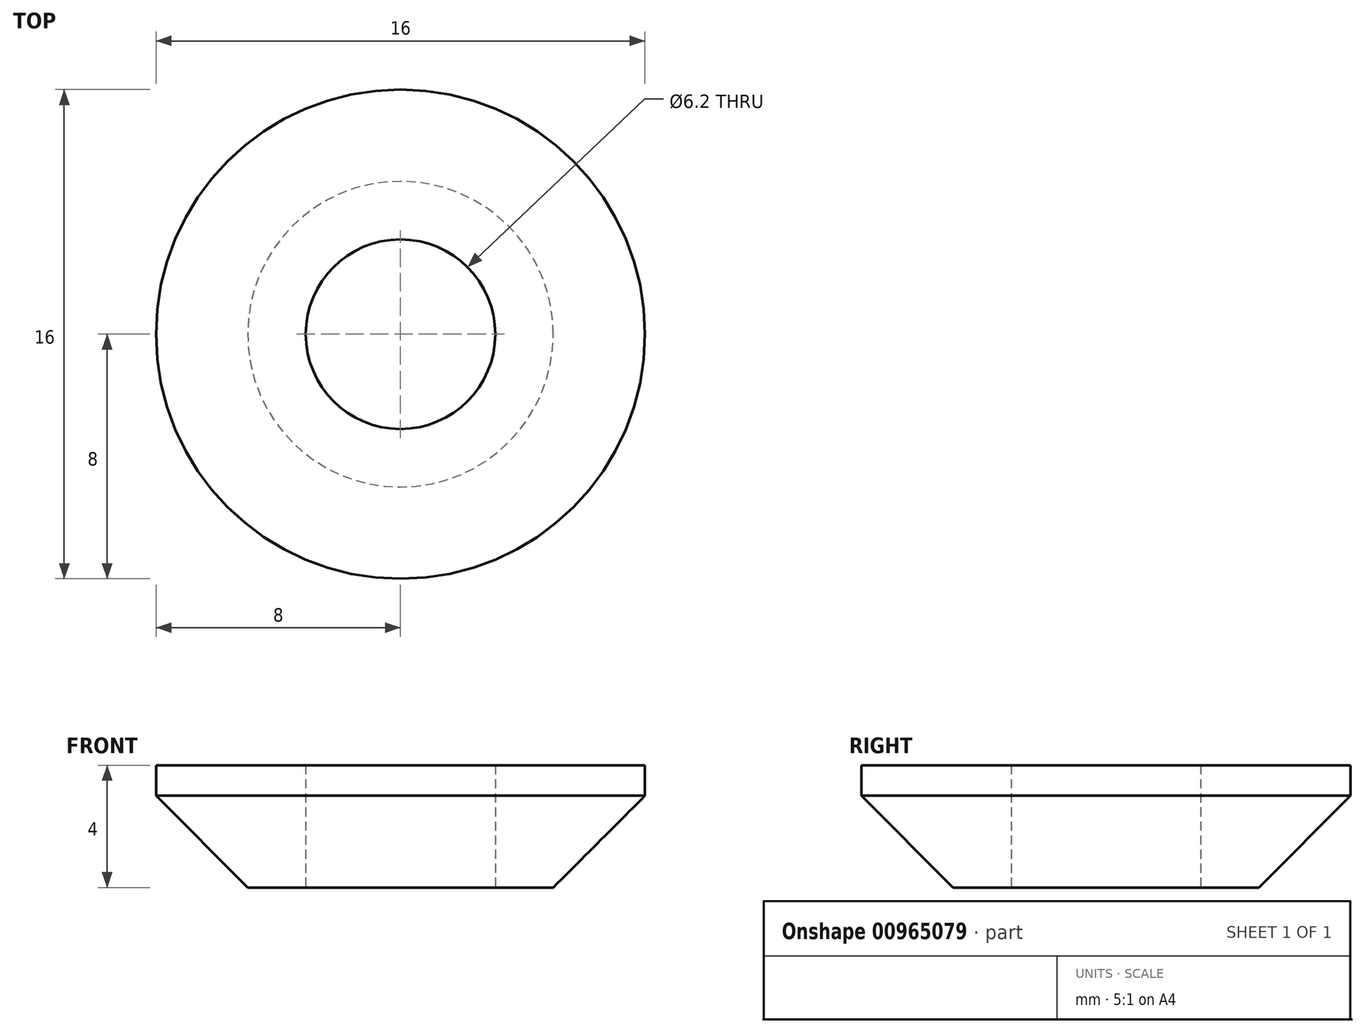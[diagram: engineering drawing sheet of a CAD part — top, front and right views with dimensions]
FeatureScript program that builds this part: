
annotation { "Feature Type Name" : "Feature", "Feature Type Description" : "" }
export const myFeature = defineFeature(function(context is Context, id is Id, definition is map)
    precondition{}
    {
        {
            var Q0;
            Q0=qCreatedBy(makeId("Top.planeOp"),FACE);
            var sketch = newSketch(context, id + "F0", { "sketchPlane" : qUnion([Q0])});
            skCircle(sketch, "E0", {"center": v(0, 0) * mm, "radius": 8 * mm});
            skCircle(sketch, "E1", {"center": v(0, 0) * mm, "radius": 3.1 * mm});
            skSolve(sketch);
        }
        {
            var Q0;
            Q0=makeQuery(id+"F0.imprint","IMPRINT",FACE,{"disambiguationData":[TD([[makeQuery(id+"F0.imprint","IMPRINT",EDGE,{"derivedFrom":sQuery(id+"F0.wireOp",EDGE,"E0")}),1.0]])]});
            extrude(context, id + "F1", {"entities" : qUnion([Q0]), "depth" : 4 * mm, "offsetDistance" : 25 * mm});
        }
        {
            var Q0;
            Q0=makeQuery(id+"F1.opExtrude","CAP_EDGE",EDGE,{"disambiguationData":[OSD([sQuery(id+"F0.wireOp",EDGE,"E0")])],"isStart":true});
            chamfer(context, id + "F2", {"entities" : qUnion([Q0]), "chamferType" : ChamferType.TWO_OFFSETS, "width1" : 3 * mm, "oppositeDirection" : false, "width2" : 3 * mm, "tangentPropagation" : true});
        }
    });
